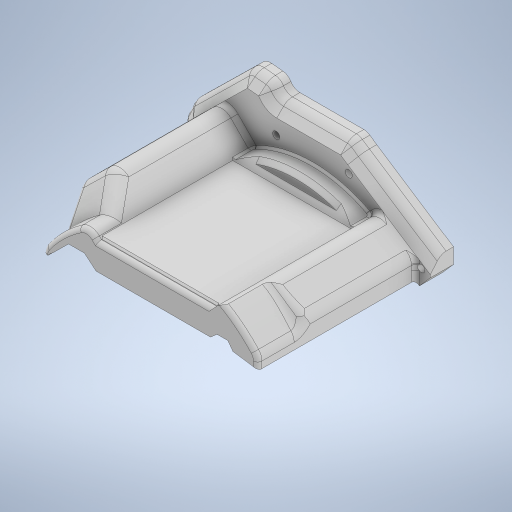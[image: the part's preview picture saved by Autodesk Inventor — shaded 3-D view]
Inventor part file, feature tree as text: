
AUTODESK INVENTOR PART (.ipt)
format: ipt  version: 2023.4 (Build 274418000, 418)  size: 1,237,504 bytes
history: native  units: mm
features: extrude x22, sketch x22, projected_geometry x17, chamfer x14, fillet x5, move_body x2, direct_edit x1
ambient origin geometry x8: Origin, YZ Plane, XZ Plane, XY Plane, X Axis, Y Axis, Z Axis, Center Point
bodies: Solid1 (feature_tree)
feature tree (83):
  extrude  "Extrusion1"  Depth=10.0mm TaperAngle=0.0deg
  extrude  "Extrusion5"  Depth=5.0mm TaperAngle=45.0deg
  extrude  "Extrusion6"  Depth=6.0mm TaperAngle=0.0deg
  chamfer  "Chamfer1"  Distance=46.0mm
  fillet  "Fillet2"  Radius=13.0mm
  extrude  "Extrusion10"  Depth=2.0mm
  extrude  "Extrusion11"  Depth=2.0mm
  extrude  "Extrusion12"  Depth=2.0mm
  extrude  "Extrusion13"  TaperAngle=0.0deg  [1 undecoded]
  extrude  "Extrusion14"  Depth=2.0mm
  direct_edit  "Direct Edit1"
  extrude  "Extrusion15"  Depth=64.0mm TaperAngle=0.0deg
  extrude  "Extrusion16"  Depth=2.0mm TaperAngle=0.0deg
  extrude  "Extrusion17"  Depth=2.0mm TaperAngle=45.0deg
  extrude  "Extrusion18"  Depth=3.3mm
  chamfer  "Chamfer2"  Distance=0.5mm Angle=45.0deg
  extrude  "Extrusion19"  Depth=13.0mm TaperAngle=45.0deg
  chamfer  "Chamfer3"  Distance=3.2mm Angle=45.0deg
  chamfer  "Chamfer4"  Distance=4.0mm
  chamfer  "Chamfer5"  Distance=4.0mm Angle=45.0deg
  fillet  "Fillet3"  Radius=2.0mm
  fillet  "Fillet4"  Radius=10.0mm
  chamfer  "Chamfer6"  Distance=2.0mm Angle=45.0deg
  fillet  "Fillet5"  Radius=40.0mm
  extrude  "Extrusion20"  Depth=8.0mm TaperAngle=45.0deg
  chamfer  "Chamfer7"  [1 undecoded]
  fillet  "Fillet6"  [1 undecoded]
  extrude  "Extrusion21"  Depth=4.0mm TaperAngle=0.0deg
  chamfer  "Chamfer8"  Distance=64.0mm
  extrude  "Extrusion22"  Depth=2.0mm TaperAngle=45.0deg
  extrude  "Extrusion23"  Depth=2.0mm TaperAngle=45.0deg
  chamfer  "Chamfer9"  Distance=2.0mm Angle=45.0deg
  extrude  "Extrusion24"  Depth=1.0mm TaperAngle=45.0deg
  extrude  "Extrusion25"  [1 undecoded]
  extrude  "Extrusion26"  [1 undecoded]
  extrude  "Extrusion27"  [1 undecoded]
  extrude  "Extrusion28"  [1 undecoded]
  chamfer  "Chamfer10"  [1 undecoded]
  chamfer  "Chamfer11"  [1 undecoded]
  chamfer  "Chamfer12"  [1 undecoded]
  chamfer  "Chamfer13"  [1 undecoded]
  chamfer  "Chamfer14"  [1 undecoded]
  sketch  "Sketch1"  dims[d0=1.0mm d1=0.0mm d10=10.0mm d11=0.0mm]
  sketch  "Sketch6"  dims[d12=0.0mm d13=0.0mm d14=5.0mm d15=2.0mm d16=45.0deg]
  projected_geometry  "Projected Loop6"
  sketch  "Sketch7"  dims[d17=6.0mm d25=6.0mm d26=0.0mm d27=46.0mm d28=0.0mm d29=13.0mm d30=0.0mm]
  sketch  "Sketch11"  dims[d31=10.0mm d32=0.0mm d33=2.0mm]
  projected_geometry  "Projected Loop10"
  sketch  "Sketch12"  dims[d34=2.0mm d35=2.0mm d36=2.0mm]
  projected_geometry  "Projected Loop11"
  projected_geometry  "Projected Loop12"
  sketch  "Sketch13"  dims[d37=2.0mm d38=2.0mm]
  projected_geometry  "Projected Loop13"
  projected_geometry  "Projected Loop14"
  sketch  "Sketch14"  dims[d39=20.0mm d40=0.0mm d41=0.0mm d42=0.0mm d43=-2.75mm]
  projected_geometry  "Projected Loop15"
  projected_geometry  "Projected Loop16"
  sketch  "Sketch15"  dims[d44=0.0mm d45=0.0mm d46=-3.75mm d47=2.0mm]
  sketch  "Sketch16"  dims[d48=3.0mm d49=64.0mm d50=0.0mm]
  projected_geometry  "Projected Loop17"
  projected_geometry  "Projected Loop18"
  sketch  "Sketch17"  dims[d51=64.0mm d52=0.0mm d53=2.0mm d54=0.0mm]
  sketch  "Sketch18"  dims[d55=7.0mm d56=0.0mm d57=2.0mm d58=2.0mm d59=45.0deg]
  sketch  "Sketch19"  dims[d60=0.0mm d61=0.0mm d62=3.3mm]
  sketch  "Sketch20"  dims[d63=3.3mm]
  sketch  "Sketch21"  dims[d64=3.3mm]
  sketch  "Sketch22"  dims[d65=3.3mm d66=0.5mm d67=2.0mm d68=45.0deg]
  projected_geometry  "Projected Loop19"
  projected_geometry  "Projected Loop20"
  sketch  "Sketch23"  dims[d69=4.0mm d70=2.0mm d71=45.0deg d72=13.0mm d73=2.0mm d74=45.0deg]
  projected_geometry  "Projected Loop21"
  sketch  "Sketch24"  dims[d75=6.0mm]
  projected_geometry  "Projected Loop22"
  sketch  "Sketch25"  dims[d76=6.0mm d77=3.2mm d78=2.0mm d79=45.0deg]
  projected_geometry  "Projected Loop23"
  sketch  "Sketch26"  dims[d80=6.0mm d81=4.0mm d82=0.0mm d83=4.0mm d84=2.0mm d85=45.0deg d86=2.0mm d87=10.0mm d88=0.0mm d89=2.0mm d90=2.0mm d91=45.0deg d92=40.0mm d93=0.0mm]
  projected_geometry  "Projected Loop24"
  sketch  "Sketch27"  dims[d94=40.0mm d95=0.0mm d96=8.0mm d97=2.0mm d98=45.0deg d99=0.0mm d100=0.0mm d101=0.0mm d102=0.0mm]
  sketch  "Sketch28"  dims[d103=4.0mm d104=0.0mm d105=4.0mm d106=0.0mm d107=64.0mm d108=0.0mm]
  projected_geometry  "Projected Loop25"
  sketch  "Sketch29"  dims[d109=0.75mm d110=2.0mm d111=45.0deg d112=2.0mm d113=2.0mm d114=45.0deg d115=2.0mm d116=2.0mm d117=45.0deg d118=2.0mm d119=2.0mm d120=45.0deg d121=1.0mm d122=2.0mm d123=45.0deg]
  move_body  "Move1"
  move_body  "Move2"
note: 12 required parameter values undecoded (feature->parameter linkage not recoverable at this tier; creation-order binding heuristic only, values carry confidence <= 0.55)
